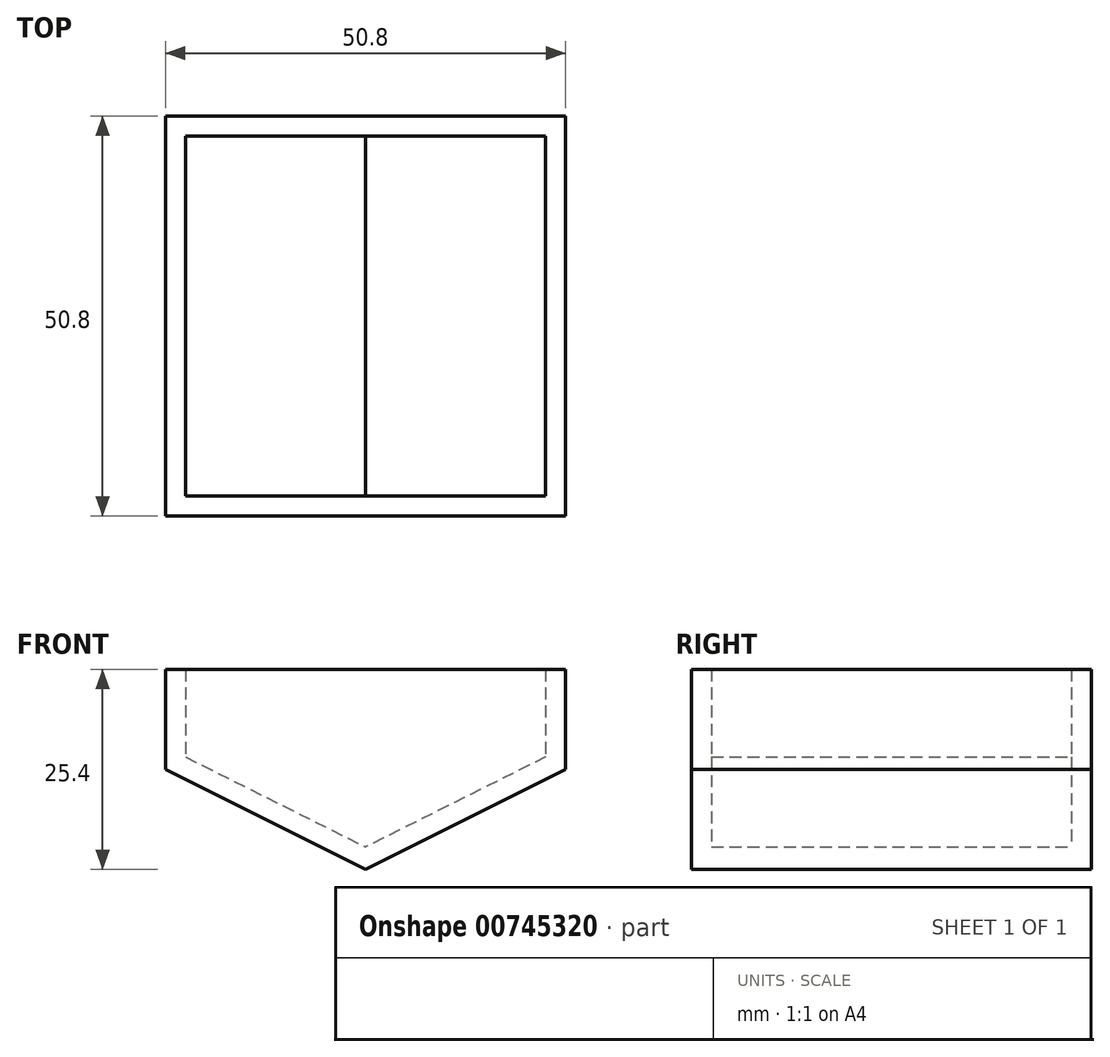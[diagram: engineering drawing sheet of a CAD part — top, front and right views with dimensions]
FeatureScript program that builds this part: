
annotation { "Feature Type Name" : "Feature", "Feature Type Description" : "" }
export const myFeature = defineFeature(function(context is Context, id is Id, definition is map)
    precondition{}
    {
        {
            var Q0;
            Q0=qCreatedBy(makeId("Front.planeOp"),FACE);
            var sketch = newSketch(context, id + "F0", { "sketchPlane" : qUnion([Q0])});
            skLineSegment(sketch, "E0", {"start": v(-54.3, 9.17) * mm, "end": v(-3.5, 9.17) * mm});
            skLineSegment(sketch, "E1", {"start": v(-28.9, -16.23) * mm, "end": v(-28.9, 9.17) * mm});
            skPoint(sketch, "E1.startSnap0", {"position": v(-28.9, 9.17) * mm});
            skLineSegment(sketch, "E2", {"start": v(-54.3, 9.17) * mm, "end": v(-54.3, -3.53) * mm});
            skLineSegment(sketch, "E3", {"start": v(-54.3, -3.53) * mm, "end": v(-28.9, -16.23) * mm});
            skLineSegment(sketch, "E4", {"start": v(-3.5, 9.17) * mm, "end": v(-3.5, -3.53) * mm});
            skPoint(sketch, "E4.endSnap0", {"position": v(-28.9, -3.53) * mm});
            skLineSegment(sketch, "E5", {"start": v(-3.5, -3.53) * mm, "end": v(-28.9, -16.23) * mm});
            skSolve(sketch);
        }
        {
            var Q0;
            {var subQ2=sQuery(id+"F0.wireOp",EDGE,"E1");Q0=makeQuery(id+"F0.imprint","IMPRINT",FACE,{"disambiguationData":[TD([[makeQuery(id+"F0.imprint","IMPRINT",EDGE,{"derivedFrom":subQ2}),1.0]])]});}
            var Q1;
            {var subQ2=sQuery(id+"F0.wireOp",EDGE,"E1");Q1=makeQuery(id+"F0.imprint","IMPRINT",FACE,{"disambiguationData":[TD([[makeQuery(id+"F0.imprint","IMPRINT",EDGE,{"derivedFrom":subQ2}),-1.0]])]});}
            extrude(context, id + "F1", {"entities" : qUnion([Q0, Q1]), "depth" : 50.8 * mm, "offsetDistance" : 25.4 * mm});
        }
        {
            var Q0;
            Q0=makeQuery(id+"F1.opExtrude","SWEPT_FACE",FACE,{"disambiguationData":[OSD([sQuery(id+"F0.wireOp",EDGE,"E0")])]});
            shell(context, id + "F2", {"entities" : qUnion([Q0]), "thickness" : 2.54 * mm});
        }
    });
